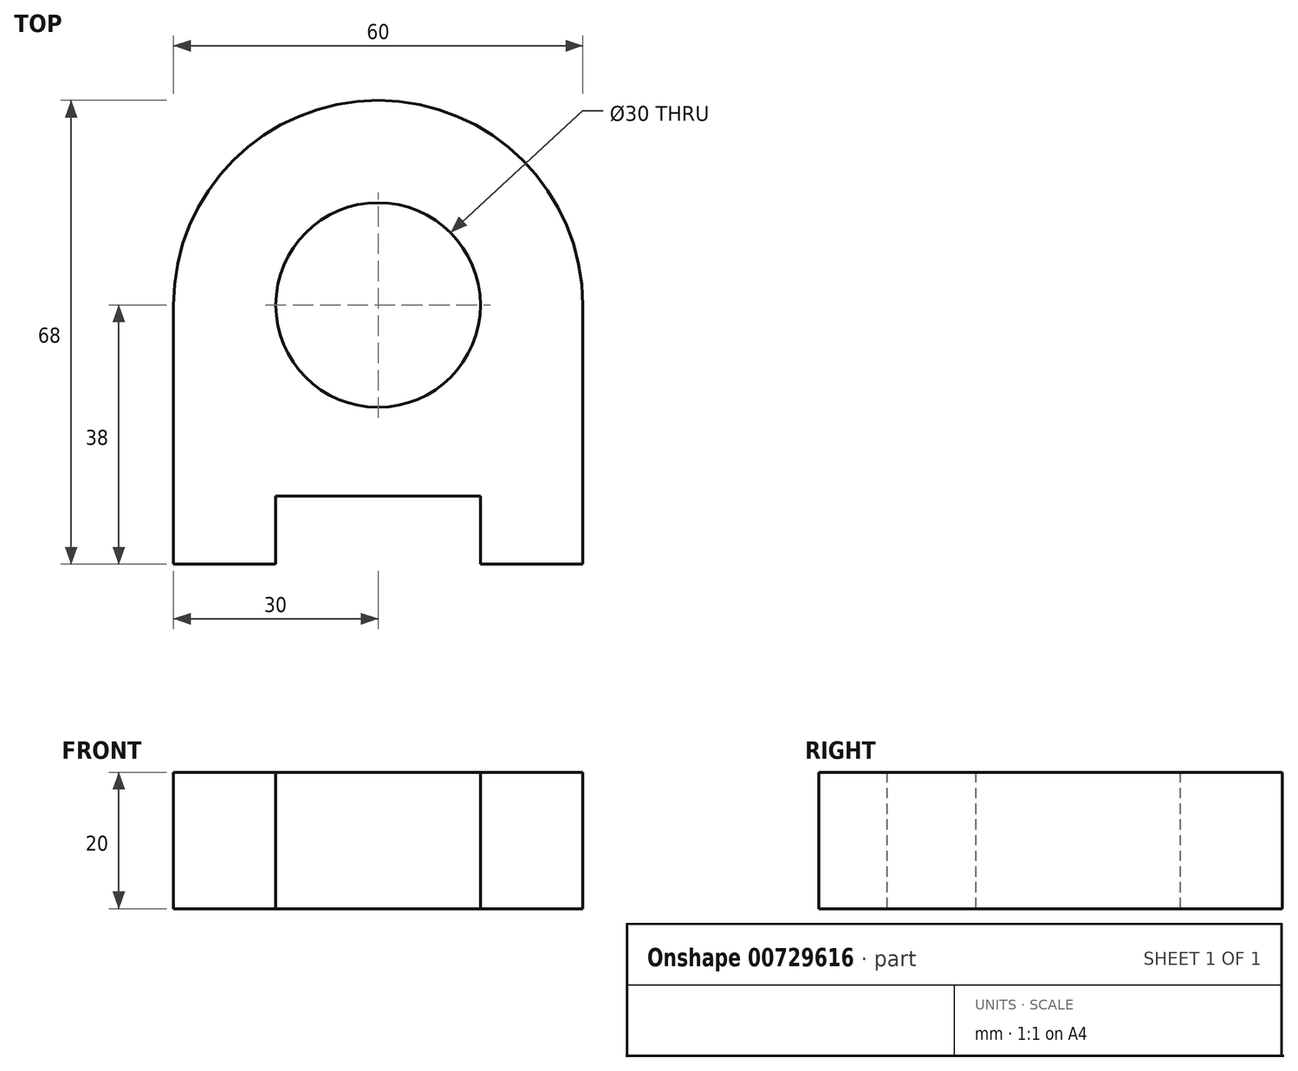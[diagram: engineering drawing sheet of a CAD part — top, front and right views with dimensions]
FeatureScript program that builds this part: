
annotation { "Feature Type Name" : "Feature", "Feature Type Description" : "" }
export const myFeature = defineFeature(function(context is Context, id is Id, definition is map)
    precondition{}
    {
        {
            var Q0;
            Q0=qCreatedBy(makeId("Top.planeOp"),FACE);
            var sketch = newSketch(context, id + "F0", { "sketchPlane" : qUnion([Q0])});
            skCircle(sketch, "E0", {"center": v(0, 0) * mm, "radius": 15 * mm});
            skArc(sketch, "E1", {"start": v(30, 0) * mm, "mid": v(0, 30) * mm, "end": v(-30, 0) * mm});
            skLineSegment(sketch, "E2.top", {"start": v(-30, -38) * mm, "end": v(-15, -38) * mm});
            skLineSegment(sketch, "E2.left", {"start": v(-30, 0) * mm, "end": v(-30, -38) * mm});
            skLineSegment(sketch, "E2.right", {"start": v(30, 0) * mm, "end": v(30, -38) * mm});
            skLineSegment(sketch, "E3.top", {"start": v(-15, -28) * mm, "end": v(15, -28) * mm});
            skLineSegment(sketch, "E3.left", {"start": v(-15, -38) * mm, "end": v(-15, -28) * mm});
            skLineSegment(sketch, "E3.right", {"start": v(15, -38) * mm, "end": v(15, -28) * mm});
            skLineSegment(sketch, "E4.trimOffspring", {"start": v(15, -38) * mm, "end": v(30, -38) * mm});
            skSolve(sketch);
        }
        {
            var Q0;
            Q0=makeQuery(id+"F0.imprint","IMPRINT",FACE,{"disambiguationData":[TD([[makeQuery(id+"F0.imprint","IMPRINT",EDGE,{"derivedFrom":sQuery(id+"F0.wireOp",EDGE,"E0")}),-1.0]])]});
            extrude(context, id + "F1", {"entities" : qUnion([Q0]), "depth" : 20 * mm, "offsetDistance" : 25 * mm});
        }
    });
